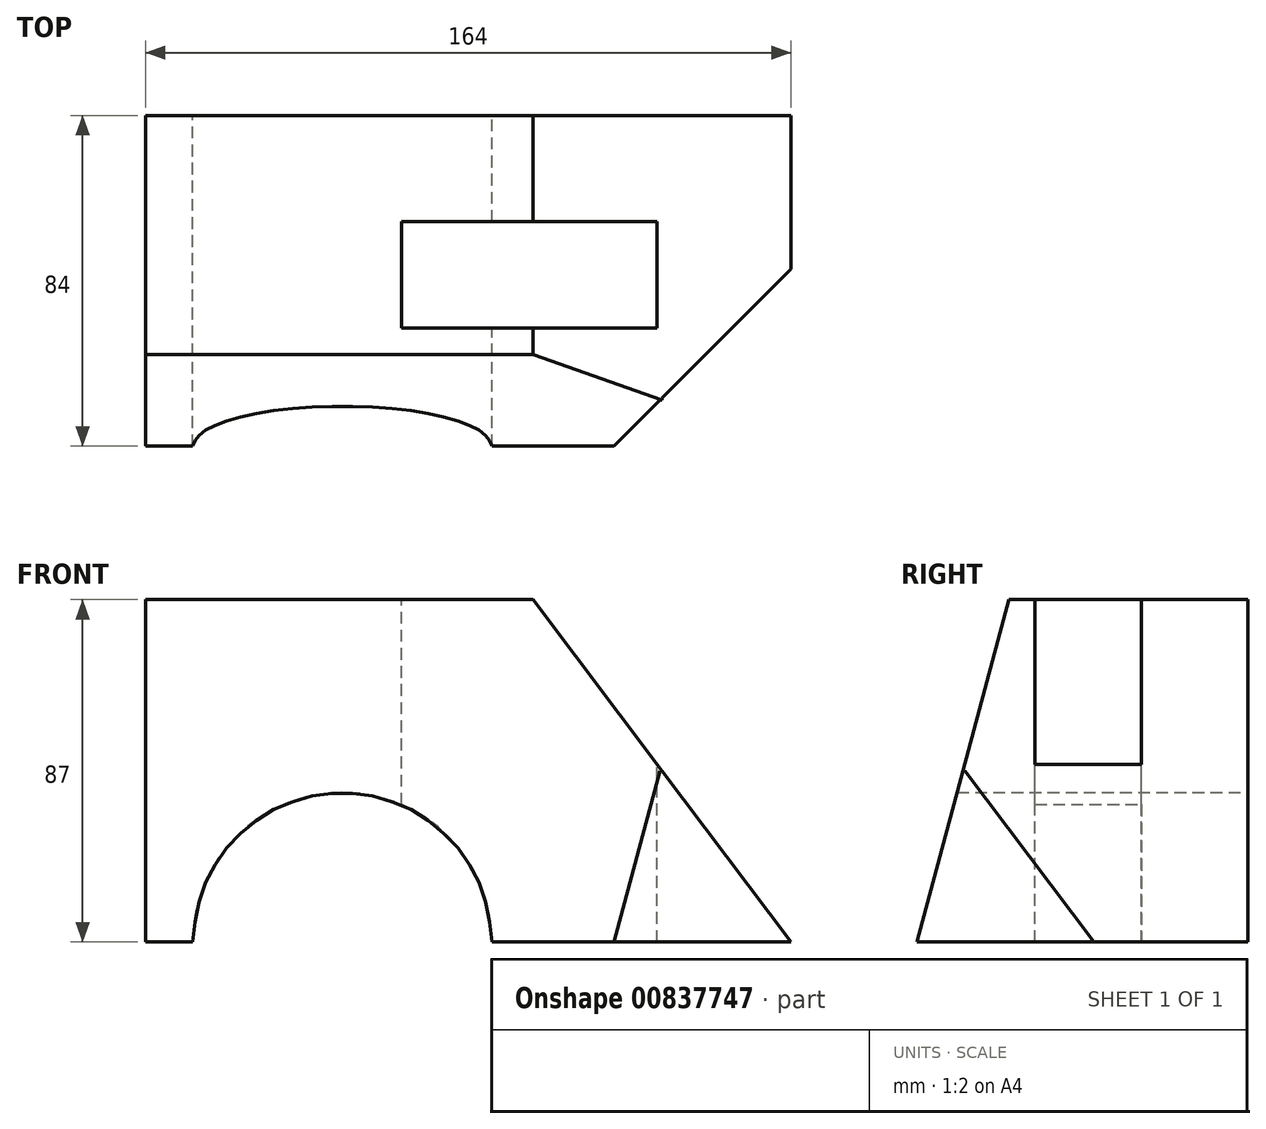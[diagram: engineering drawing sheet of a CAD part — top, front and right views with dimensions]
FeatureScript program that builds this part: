
annotation { "Feature Type Name" : "Feature", "Feature Type Description" : "" }
export const myFeature = defineFeature(function(context is Context, id is Id, definition is map)
    precondition{}
    {
        {
            var Q0;
            Q0=qCreatedBy(makeId("Front.planeOp"),FACE);
            var sketch = newSketch(context, id + "F0", { "sketchPlane" : qUnion([Q0])});
            skLineSegment(sketch, "E0.bottom", {"start": v(82, 43.5) * mm, "end": v(-82, 43.5) * mm});
            skLineSegment(sketch, "E0.top", {"start": v(82, -43.5) * mm, "end": v(-82, -43.5) * mm});
            skLineSegment(sketch, "E0.left", {"start": v(82, 43.5) * mm, "end": v(82, -43.5) * mm});
            skLineSegment(sketch, "E0.right", {"start": v(-82, 43.5) * mm, "end": v(-82, -43.5) * mm});
            skPoint(sketch, "E0.middle", {"position": v(0, 0) * mm});
            skLineSegment(sketch, "E1", {"start": v(82, -43.5) * mm, "end": v(16.44, 43.5) * mm});
            skLineSegment(sketch, "E2", {"start": v(-82, -43.5) * mm, "end": v(-32, -43.5) * mm});
            skArc(sketch, "E3", {"start": v(6, -43.5) * mm, "mid": v(-32, -5.5) * mm, "end": v(-70, -43.5) * mm});
            skPoint(sketch, "E4", {"position": v(0, 43.5) * mm});
            skLineSegment(sketch, "E5", {"start": v(0, 43.5) * mm, "end": v(16.44, 43.5) * mm});
            skSolve(sketch);
        }
        {
            var Q0;
            {var subQ0=sQuery(id+"F0.wireOp",EDGE,"E0.right");Q0=makeQuery(id+"F0.imprint","IMPRINT",FACE,{"disambiguationData":[TD([[makeQuery(id+"F0.imprint","IMPRINT",EDGE,{"derivedFrom":subQ0}),1.0]])]});}
            extrude(context, id + "F1", {"entities" : qUnion([Q0]), "depth" : 84 * mm, "offsetDistance" : 25 * mm});
        }
        {
            var Q0;
            Q0=makeQuery(id+"F1.opExtrude","SWEPT_FACE",FACE,{"disambiguationData":[OSD([sQuery(id+"F0.wireOp",EDGE,"E0.bottom"),sQuery(id+"F0.wireOp",EDGE,"E5")])]});
            var sketch = newSketch(context, id + "F2", { "sketchPlane" : qUnion([Q0])});
            skLineSegment(sketch, "E6.0.0", {"start": v(16.44, 0) * mm, "end": v(-82, 0) * mm});
            skLineSegment(sketch, "E6.0.1", {"start": v(-82, 0) * mm, "end": v(-82, -84) * mm});
            skLineSegment(sketch, "E6.0.2", {"start": v(-82, -84) * mm, "end": v(16.44, -84) * mm});
            skLineSegment(sketch, "E6.0.3", {"start": v(16.44, -84) * mm, "end": v(16.44, 0) * mm});
            skLineSegment(sketch, "E7", {"start": v(-82, 0) * mm, "end": v(-82, -14) * mm});
            skLineSegment(sketch, "E8", {"start": v(-82, -14) * mm, "end": v(-82, -39) * mm});
            skLineSegment(sketch, "E9", {"start": v(-82, -39) * mm, "end": v(-48, -39) * mm});
            skLineSegment(sketch, "E10", {"start": v(-48, -39) * mm, "end": v(-48, -14) * mm});
            skLineSegment(sketch, "E11", {"start": v(-48, -14) * mm, "end": v(-82, -14) * mm});
            skLineSegment(sketch, "E12.0.0", {"start": v(82, 0) * mm, "end": v(16.44, 0) * mm});
            skLineSegment(sketch, "E12.0.1", {"start": v(16.44, 0) * mm, "end": v(16.44, -84) * mm});
            skLineSegment(sketch, "E12.0.2", {"start": v(16.44, -84) * mm, "end": v(82, -84) * mm});
            skLineSegment(sketch, "E12.0.3", {"start": v(82, -84) * mm, "end": v(82, 0) * mm});
            skPoint(sketch, "E13.0", {"position": v(82, 0) * mm});
            skLineSegment(sketch, "E14", {"start": v(82, 0) * mm, "end": v(48, 0) * mm});
            skLineSegment(sketch, "E15", {"start": v(48, 0) * mm, "end": v(-17, 0) * mm});
            skLineSegment(sketch, "E16", {"start": v(-17, 0) * mm, "end": v(-17, -27) * mm});
            skLineSegment(sketch, "E17", {"start": v(-17, -27) * mm, "end": v(-17, -54) * mm});
            skLineSegment(sketch, "E18", {"start": v(-17, -54) * mm, "end": v(48, -54) * mm});
            skLineSegment(sketch, "E19", {"start": v(48, -54) * mm, "end": v(48, -27) * mm});
            skLineSegment(sketch, "E20", {"start": v(48, -27) * mm, "end": v(-17, -27) * mm});
            skSolve(sketch);
        }
        {
            var Q0;
            {var subQ5=sQuery(id+"F2.wireOp",EDGE,"E19");Q0=makeQuery(id+"F2.imprint","IMPRINT",FACE,{"disambiguationData":[TD([[makeQuery(id+"F2.imprint","IMPRINT",EDGE,{"derivedFrom":subQ5}),1.0]])]});}
            var Q1;
            {var subQ5=sQuery(id+"F2.wireOp",EDGE,"E17");Q1=makeQuery(id+"F2.imprint","IMPRINT",FACE,{"disambiguationData":[TD([[makeQuery(id+"F2.imprint","IMPRINT",EDGE,{"derivedFrom":subQ5}),1.0]])]});}
            var Q2;
            Q2=makeQuery(id+"F2.imprint","IMPRINT",FACE,{"disambiguationData":[TD([[makeQuery(id+"F2.imprint","IMPRINT",EDGE,{"derivedFrom":sQuery(id+"F2.wireOp",EDGE,"E8")}),-1.0]])]});
            extrude(context, id + "F3", {"entities" : qUnion([Q0, Q1, Q2]), "operationType" : NewBodyOperationType.REMOVE, "oppositeDirection" : true, "depth" : 187.4 * mm, "offsetDistance" : 25 * mm});
        }
        {
            var Q0;
            Q0=qCreatedBy(makeId("Right.planeOp"),FACE);
            var sketch = newSketch(context, id + "F4", { "sketchPlane" : qUnion([Q0])});
            skLineSegment(sketch, "E21.0.0", {"start": v(-27, 1.62) * mm, "end": v(-54, 1.62) * mm});
            skLineSegment(sketch, "E21.0.1", {"start": v(-54, 1.62) * mm, "end": v(-54, 43.5) * mm});
            skLineSegment(sketch, "E21.0.2", {"start": v(-54, 43.5) * mm, "end": v(-84, 43.5) * mm});
            skLineSegment(sketch, "E21.0.3", {"start": v(-84, 43.5) * mm, "end": v(-84, -43.5) * mm});
            skLineSegment(sketch, "E21.0.4", {"start": v(-84, -43.5) * mm, "end": v(0, -43.5) * mm});
            skLineSegment(sketch, "E21.0.5", {"start": v(0, -43.5) * mm, "end": v(0, 43.5) * mm});
            skLineSegment(sketch, "E21.0.6", {"start": v(0, 43.5) * mm, "end": v(-27, 43.5) * mm});
            skLineSegment(sketch, "E21.0.7", {"start": v(-27, 43.5) * mm, "end": v(-27, 1.62) * mm});
            skLineSegment(sketch, "E22", {"start": v(-84, -43.5) * mm, "end": v(-57.55, 55.2) * mm});
            skSolve(sketch);
        }
        {
            var Q0;
            {var subQ0=sQuery(id+"F4.wireOp",EDGE,"E21.0.3");Q0=makeQuery(id+"F4.imprint","IMPRINT",FACE,{"disambiguationData":[TD([[makeQuery(id+"F4.imprint","IMPRINT",EDGE,{"derivedFrom":subQ0}),1.0]])]});}
            extrude(context, id + "F5", {"entities" : qUnion([Q0]), "operationType" : NewBodyOperationType.REMOVE, "depth" : 299 * mm, "offsetDistance" : 25 * mm, "hasSecondDirection" : true, "secondDirectionOppositeDirection" : true, "secondDirectionDepth" : 323 * mm});
        }
        {
            var Q0;
            Q0=qCreatedBy(makeId("Top.planeOp"),FACE);
            var sketch = newSketch(context, id + "F6", { "sketchPlane" : qUnion([Q0])});
            skLineSegment(sketch, "E23.0.0", {"start": v(-82, -60.69) * mm, "end": v(-82, -84) * mm});
            skLineSegment(sketch, "E23.0.1", {"start": v(-82, -84) * mm, "end": v(-70, -84) * mm});
            skEllipticalArc(sketch, "E23.0.2", {});
            skLineSegment(sketch, "E23.0.3", {"start": v(6, -84) * mm, "end": v(82, -84) * mm});
            skLineSegment(sketch, "E23.0.4", {"start": v(82, -84) * mm, "end": v(16.44, -60.69) * mm});
            skLineSegment(sketch, "E23.0.5", {"start": v(16.44, -60.69) * mm, "end": v(-82, -60.69) * mm});
            skPoint(sketch, "E24.0", {"position": v(82, 0) * mm});
            skLineSegment(sketch, "E25", {"start": v(82, 0) * mm, "end": v(82, -39) * mm});
            skLineSegment(sketch, "E26", {"start": v(82, -39) * mm, "end": v(37, -84) * mm});
            skLineSegment(sketch, "E27", {"start": v(82, -84) * mm, "end": v(37, -84) * mm});
            skLineSegment(sketch, "E28", {"start": v(37, -84) * mm, "end": v(82, -84) * mm});
            skLineSegment(sketch, "E29", {"start": v(82, -39) * mm, "end": v(82, -84) * mm});
            const initialGuessF6  = {"E23.0.2": [-0.032, -0.084, 1, 0, 0.038, 0.01018206931238265, 0, 3.141592653589793]};
            skSetInitialGuess(sketch, initialGuessF6);
            skSolve(sketch);
        }
        {
            var Q0;
            {var subQ0=sQuery(id+"F6.wireOp",EDGE,"E26");var subQ1=sQuery(id+"F6.wireOp",EDGE,"E23.0.3");var subQ2=makeQuery(id+"F6.imprint","INTERSECT",VERTEX,{"derivedFrom":[subQ1,subQ0]});Q0=makeQuery(id+"F6.imprint","IMPRINT",FACE,{"disambiguationData":[TD([[makeQuery(id+"F6.imprint","IMPRINT",EDGE,{"disambiguationData":[TD([[subQ2,1.0]])],"derivedFrom":subQ0}),1.0]])]});}
            var Q1;
            {var subQ0=sQuery(id+"F6.wireOp",EDGE,"E29");Q1=makeQuery(id+"F6.imprint","IMPRINT",FACE,{"disambiguationData":[TD([[makeQuery(id+"F6.imprint","IMPRINT",EDGE,{"derivedFrom":subQ0}),-1.0]])]});}
            extrude(context, id + "F7", {"entities" : qUnion([Q0, Q1]), "operationType" : NewBodyOperationType.REMOVE, "oppositeDirection" : true, "depth" : 75.8 * mm, "offsetDistance" : 25 * mm});
        }
    });
